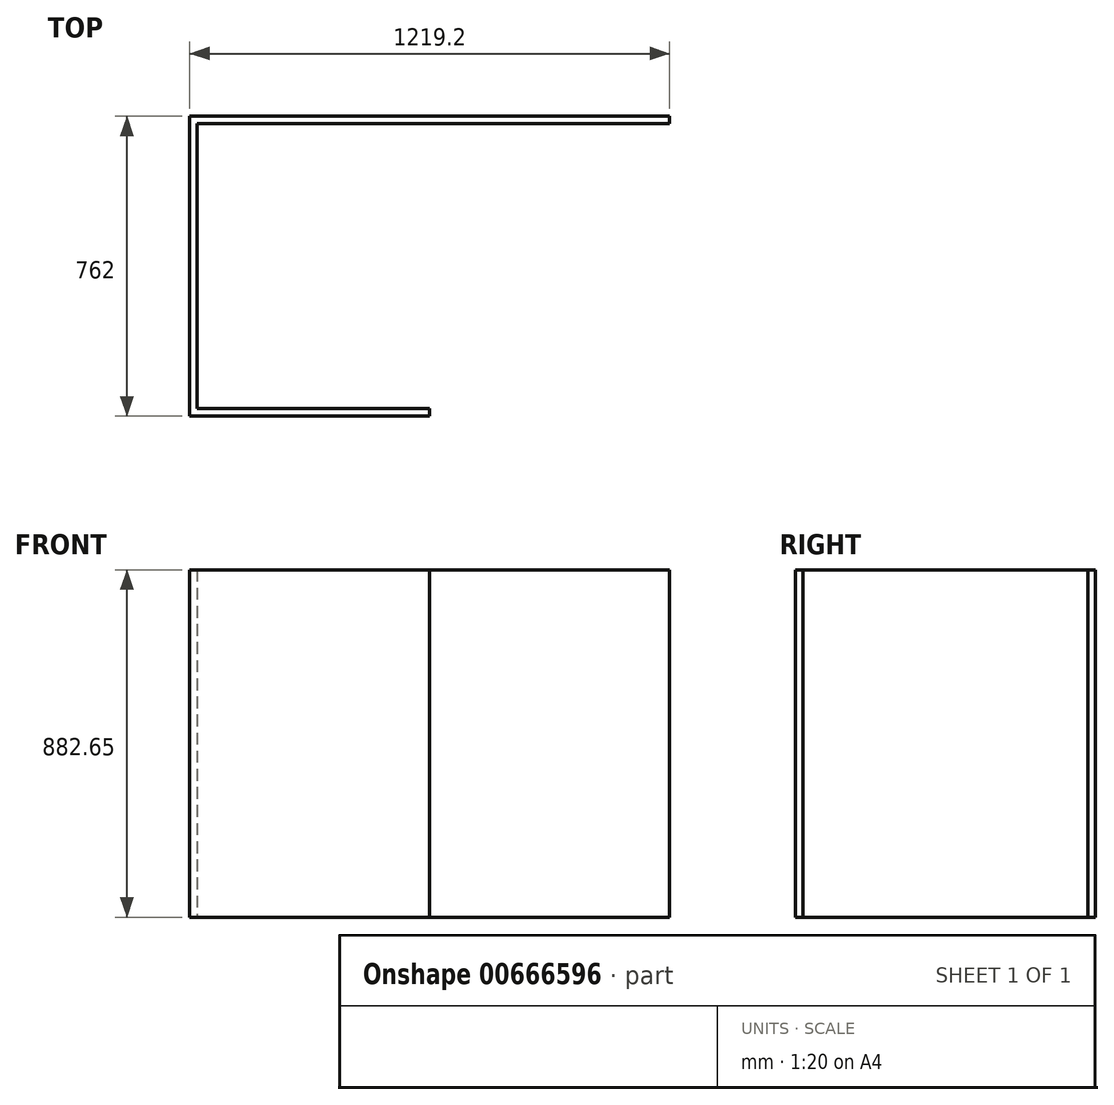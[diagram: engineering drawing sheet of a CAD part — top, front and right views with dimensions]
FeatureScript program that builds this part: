
annotation { "Feature Type Name" : "Feature", "Feature Type Description" : "" }
export const myFeature = defineFeature(function(context is Context, id is Id, definition is map)
    precondition{}
    {
        {
            var Q0;
            Q0=qCreatedBy(makeId("Top.planeOp"),FACE);
            var sketch = newSketch(context, id + "F0", { "sketchPlane" : qUnion([Q0])});
            skLineSegment(sketch, "E0.bottom", {"start": v(-609.6, 381) * mm, "end": v(609.6, 381) * mm});
            skLineSegment(sketch, "E0.top", {"start": v(-609.6, -381) * mm, "end": v(609.6, -381) * mm});
            skLineSegment(sketch, "E0.left", {"start": v(-609.6, 381) * mm, "end": v(-609.6, -381) * mm});
            skLineSegment(sketch, "E0.right", {"start": v(609.6, 381) * mm, "end": v(609.6, -381) * mm});
            skPoint(sketch, "E0.middle", {"position": v(0, 0) * mm});
            skLineSegment(sketch, "E1.bottom", {"start": v(-590.55, 361.95) * mm, "end": v(590.55, 361.95) * mm});
            skLineSegment(sketch, "E1.top", {"start": v(-590.55, -361.95) * mm, "end": v(590.55, -361.95) * mm});
            skLineSegment(sketch, "E1.left", {"start": v(-590.55, 361.95) * mm, "end": v(-590.55, -361.95) * mm});
            skLineSegment(sketch, "E1.right", {"start": v(590.55, 361.95) * mm, "end": v(590.55, -361.95) * mm});
            skLineSegment(sketch, "E2", {"start": v(590.55, 361.95) * mm, "end": v(609.6, 361.95) * mm});
            skLineSegment(sketch, "E3", {"start": v(590.55, -361.95) * mm, "end": v(609.6, -361.95) * mm});
            skLineSegment(sketch, "E4.bottom", {"start": v(609.6, -381) * mm, "end": v(0, -381) * mm});
            skLineSegment(sketch, "E4.top", {"start": v(609.6, -361.95) * mm, "end": v(0, -361.95) * mm});
            skLineSegment(sketch, "E4.left", {"start": v(609.6, -381) * mm, "end": v(609.6, -361.95) * mm});
            skLineSegment(sketch, "E4.right", {"start": v(0, -381) * mm, "end": v(0, -361.95) * mm});
            skSolve(sketch);
        }
        {
            var Q0;
            {var subQ1=sQuery(id+"F0.wireOp",EDGE,"E0.bottom");Q0=makeQuery(id+"F0.imprint","IMPRINT",FACE,{"disambiguationData":[TD([[makeQuery(id+"F0.imprint","IMPRINT",EDGE,{"derivedFrom":subQ1}),-1.0]])]});}
            extrude(context, id + "F1", {"entities" : qUnion([Q0]), "depth" : 882.65 * mm, "offsetDistance" : 25.4 * mm});
        }
    });
